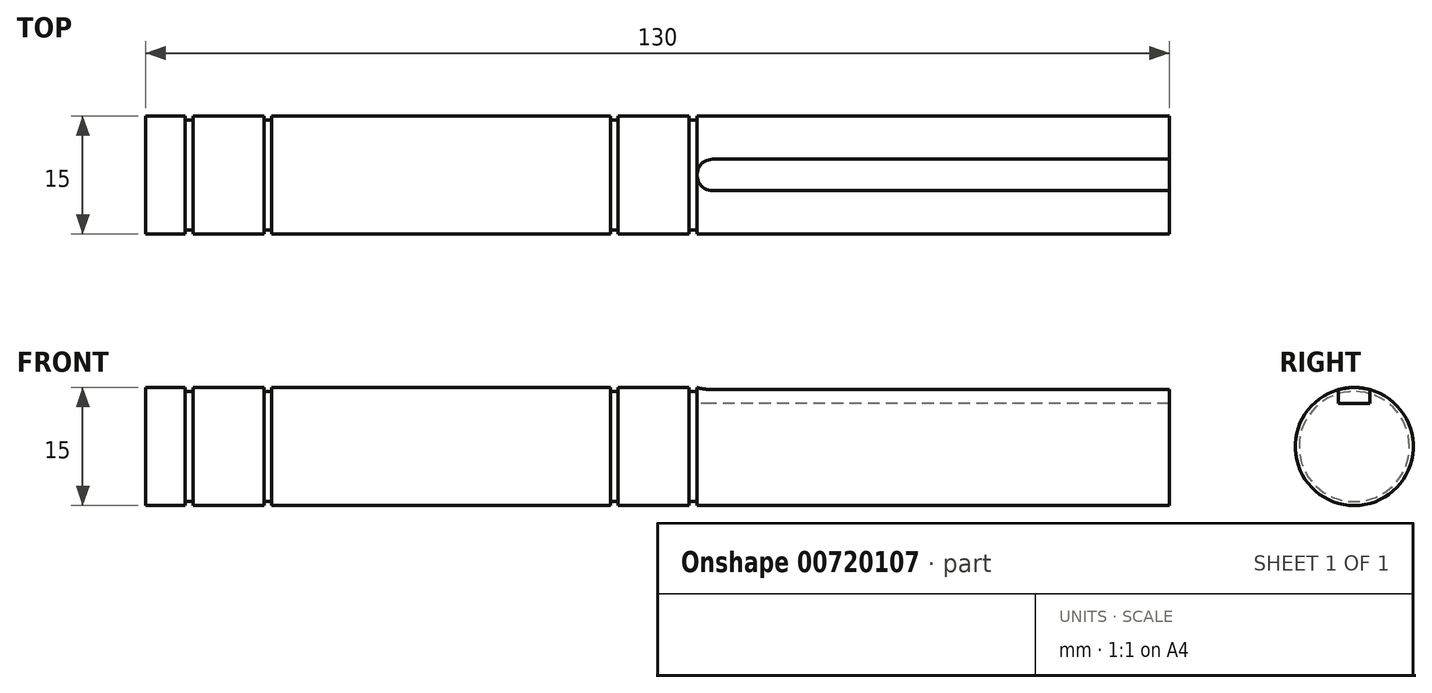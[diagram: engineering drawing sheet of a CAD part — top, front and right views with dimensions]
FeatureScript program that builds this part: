
annotation { "Feature Type Name" : "Feature", "Feature Type Description" : "" }
export const myFeature = defineFeature(function(context is Context, id is Id, definition is map)
    precondition{}
    {
        {
            var Q0;
            Q0=qCreatedBy(makeId("Front.planeOp"),FACE);
            var sketch = newSketch(context, id + "F0", { "sketchPlane" : qUnion([Q0])});
            skLineSegment(sketch, "E0", {"start": v(0, 0) * mm, "end": v(0, 7.5) * mm});
            skLineSegment(sketch, "E1", {"start": v(0, 7.5) * mm, "end": v(5, 7.5) * mm});
            skLineSegment(sketch, "E2", {"start": v(5, 7.5) * mm, "end": v(5, 7) * mm});
            skLineSegment(sketch, "E3", {"start": v(5, 7) * mm, "end": v(6, 7) * mm});
            skLineSegment(sketch, "E4", {"start": v(6, 7) * mm, "end": v(6, 7.5) * mm});
            skLineSegment(sketch, "E5", {"start": v(6, 7.5) * mm, "end": v(15, 7.5) * mm});
            skLineSegment(sketch, "E6", {"start": v(15, 7.5) * mm, "end": v(15, 7) * mm});
            skLineSegment(sketch, "E7", {"start": v(15, 7) * mm, "end": v(16, 7) * mm});
            skLineSegment(sketch, "E8", {"start": v(16, 7) * mm, "end": v(16, 7.5) * mm});
            skLineSegment(sketch, "E9", {"start": v(16, 7.5) * mm, "end": v(59, 7.5) * mm});
            skLineSegment(sketch, "E10", {"start": v(59, 7.5) * mm, "end": v(59, 7) * mm});
            skLineSegment(sketch, "E11", {"start": v(59, 7) * mm, "end": v(60, 7) * mm});
            skLineSegment(sketch, "E12", {"start": v(60, 7) * mm, "end": v(60, 7.5) * mm});
            skLineSegment(sketch, "E13", {"start": v(60, 7.5) * mm, "end": v(69, 7.5) * mm});
            skLineSegment(sketch, "E14", {"start": v(69, 7.5) * mm, "end": v(69, 7) * mm});
            skLineSegment(sketch, "E15", {"start": v(69, 7) * mm, "end": v(70, 7) * mm});
            skLineSegment(sketch, "E16", {"start": v(70, 7) * mm, "end": v(70, 7.5) * mm});
            skLineSegment(sketch, "E17", {"start": v(70, 7.5) * mm, "end": v(130, 7.5) * mm});
            skLineSegment(sketch, "E18", {"start": v(130, 7.5) * mm, "end": v(130, 0) * mm});
            skLineSegment(sketch, "E19", {"start": v(130, 0) * mm, "end": v(0, 0) * mm});
            skSolve(sketch);
        }
        {
            var Q0;
            Q0=makeQuery(id+"F0.imprint","IMPRINT",FACE,{"disambiguationData":[TD([[makeQuery(id+"F0.imprint","IMPRINT",EDGE,{"derivedFrom":sQuery(id+"F0.wireOp",EDGE,"E0")}),-1.0]])]});
            var Q1;
            Q1=sQuery(id+"F0.wireOp",EDGE,"E19");
            revolve(context, id + "F1", {"surfaceOperationType" : NewSurfaceOperationType.NEW, "entities" : qUnion([Q0]), "axis" : qUnion([Q1]), "revolveType" : RevolveType.FULL});
        }
        {
            var Q0;
            Q0=qCreatedBy(makeId("Top.planeOp"),FACE);
            cPlane(context, id + "F2", {"entities" : qUnion([Q0]), "cplaneType" : CPlaneType.OFFSET, "offset" : 7.5 * mm, "width" : 150 * mm, "height" : 150 * mm});
        }
        {
            var Q0;
            Q0=qCreatedBy(id+"F2.planeOp",FACE);
            var sketch = newSketch(context, id + "F3", { "sketchPlane" : qUnion([Q0])});
            skLineSegment(sketch, "E20", {"start": v(130, 0) * mm, "end": v(130, 2) * mm});
            skLineSegment(sketch, "E21", {"start": v(130, 2) * mm, "end": v(72, 2) * mm});
            skLineSegment(sketch, "E22", {"start": v(130, -2) * mm, "end": v(130, 0) * mm});
            skLineSegment(sketch, "E23", {"start": v(130, -2) * mm, "end": v(72, -2) * mm});
            skArc(sketch, "E24", {"start": v(72, 2) * mm, "mid": v(70, 0) * mm, "end": v(72, -2) * mm});
            skPoint(sketch, "E24.centerSnap0", {"position": v(70, 0) * mm});
            skSolve(sketch);
        }
        {
            var Q0;
            Q0=qSketchRegion(id+"F3",true);
            extrude(context, id + "F4", {"entities" : qUnion([Q0]), "operationType" : NewBodyOperationType.REMOVE, "oppositeDirection" : true, "depth" : 2 * mm, "offsetDistance" : 25 * mm});
        }
    });
